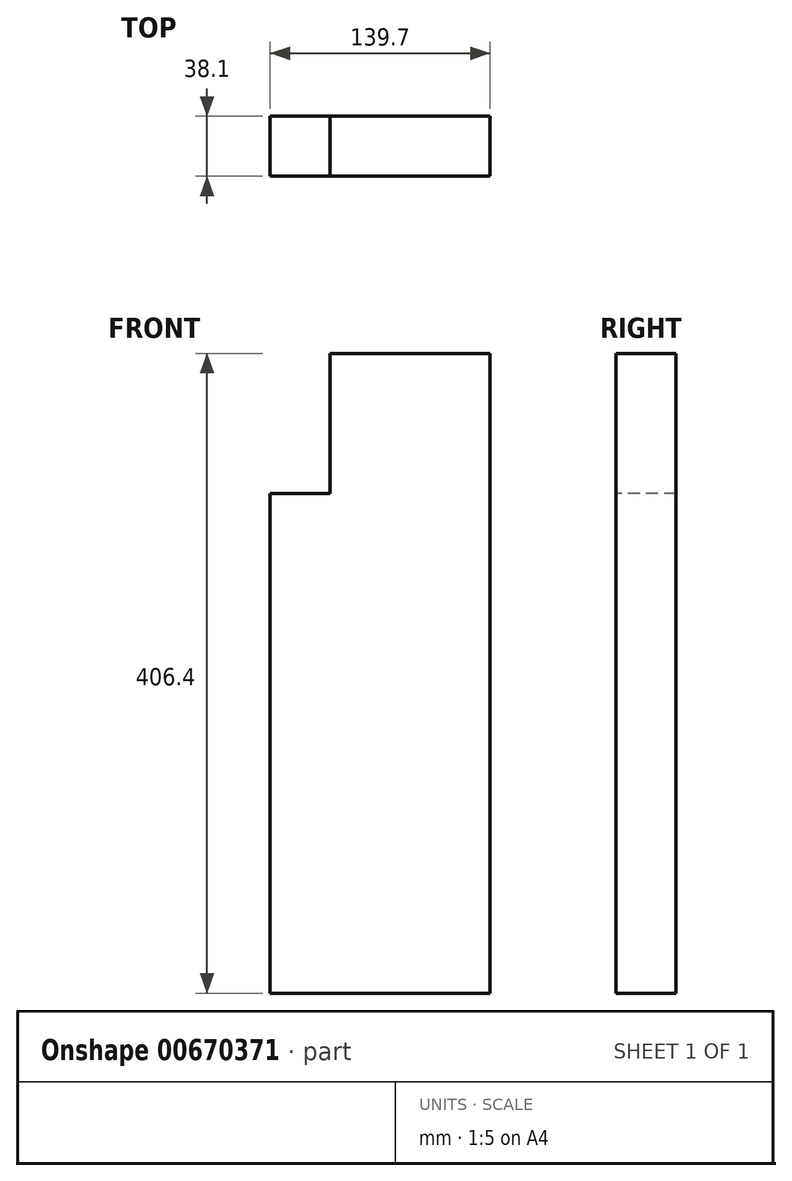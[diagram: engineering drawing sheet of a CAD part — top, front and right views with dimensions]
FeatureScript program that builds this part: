
annotation { "Feature Type Name" : "Feature", "Feature Type Description" : "" }
export const myFeature = defineFeature(function(context is Context, id is Id, definition is map)
    precondition{}
    {
        {
            var Q0;
            Q0=qCreatedBy(makeId("Right.planeOp"),FACE);
            var sketch = newSketch(context, id + "F0", { "sketchPlane" : qUnion([Q0])});
            skLineSegment(sketch, "E0.bottom", {"start": v(0, 0) * mm, "end": v(38.1, 0) * mm});
            skLineSegment(sketch, "E0.top", {"start": v(0, -406.4) * mm, "end": v(38.1, -406.4) * mm});
            skLineSegment(sketch, "E0.left", {"start": v(0, 0) * mm, "end": v(0, -406.4) * mm});
            skLineSegment(sketch, "E0.right", {"start": v(38.1, 0) * mm, "end": v(38.1, -406.4) * mm});
            skSolve(sketch);
        }
        {
            var Q0;
            Q0 = qSketchRegion(id + "F0", true);
            extrude(context, id + "F1", {"entities" : qUnion([Q0]), "depth" : 139.7 * mm, "offsetDistance" : 25.4 * mm});
        }
        {
            var Q0;
            Q0=makeQuery(id+"F1.opExtrude","SWEPT_FACE",FACE,{"disambiguationData":[OSD([sQuery(id+"F0.wireOp",EDGE,"E0.left")])]});
            var sketch = newSketch(context, id + "F2", { "sketchPlane" : qUnion([Q0])});
            skLineSegment(sketch, "E1.bottom", {"start": v(0, 0) * mm, "end": v(38.1, 0) * mm});
            skLineSegment(sketch, "E1.top", {"start": v(0, -88.9) * mm, "end": v(38.1, -88.9) * mm});
            skLineSegment(sketch, "E1.left", {"start": v(0, 0) * mm, "end": v(0, -88.9) * mm});
            skLineSegment(sketch, "E1.right", {"start": v(38.1, 0) * mm, "end": v(38.1, -88.9) * mm});
            skSolve(sketch);
        }
        {
            var Q0;
            Q0 = qSketchRegion(id + "F2", true);
            extrude(context, id + "F3", {"entities" : qUnion([Q0]), "operationType" : NewBodyOperationType.REMOVE, "endBound" : BoundingType.UP_TO_NEXT, "oppositeDirection" : true, "depth" : 25.4 * mm, "offsetDistance" : 25.4 * mm});
        }
    });
